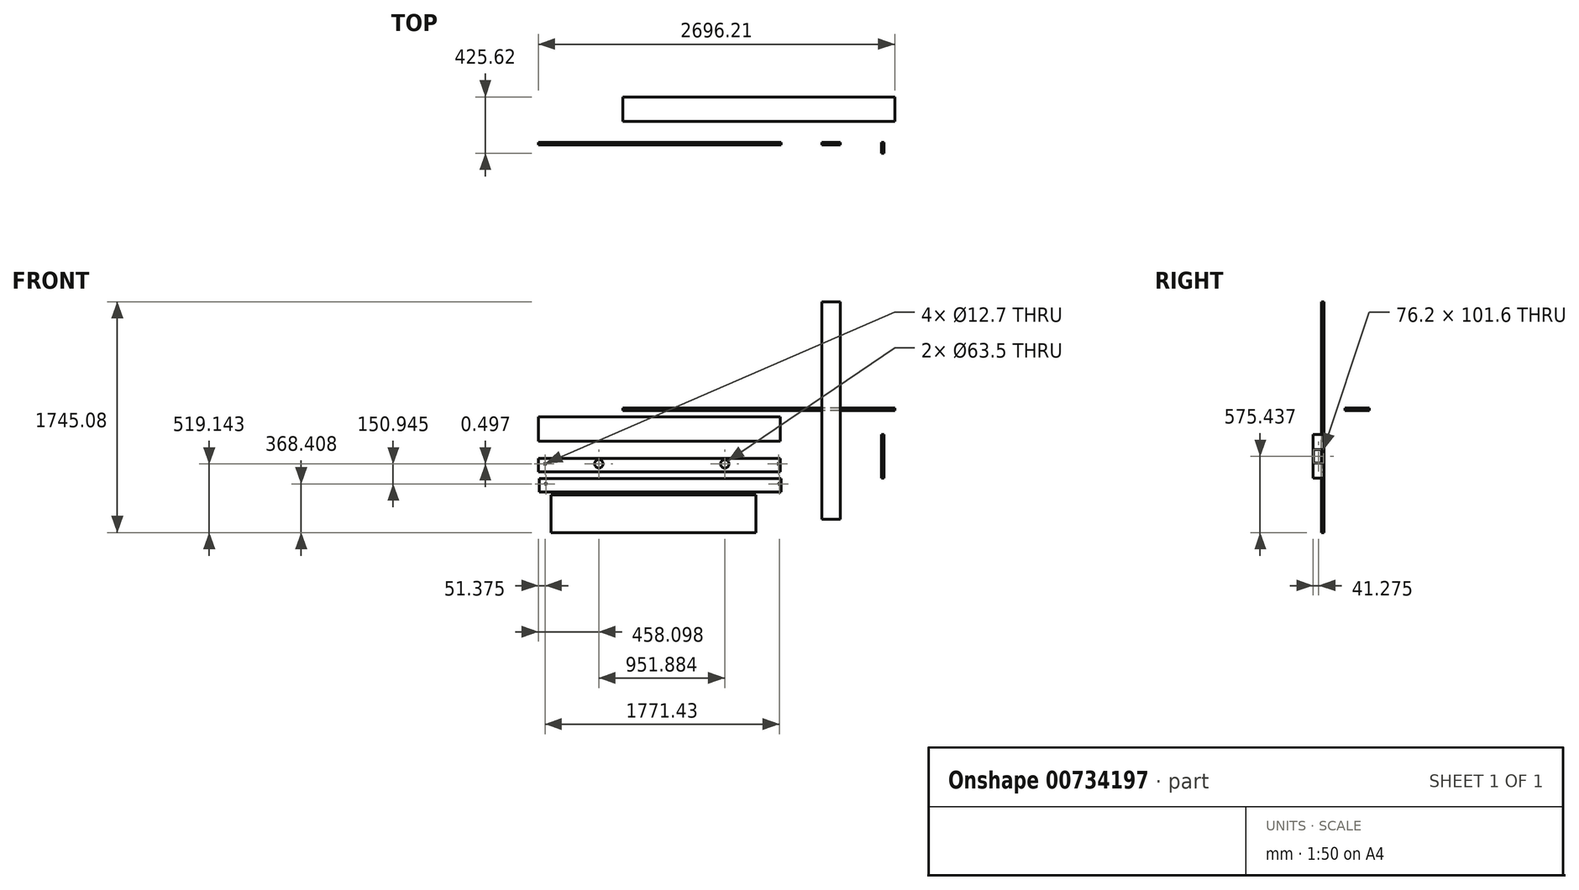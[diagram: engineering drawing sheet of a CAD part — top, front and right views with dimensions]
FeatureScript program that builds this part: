
annotation { "Feature Type Name" : "Feature", "Feature Type Description" : "" }
export const myFeature = defineFeature(function(context is Context, id is Id, definition is map)
    precondition{}
    {
        {
            var Q0;
            Q0=qCreatedBy(makeId("Front.planeOp"),FACE);
            var sketch = newSketch(context, id + "F0", { "sketchPlane" : qUnion([Q0])});
            skLineSegment(sketch, "E0.bottom", {"start": v(69.85, -822.32) * mm, "end": v(-69.85, -822.32) * mm});
            skLineSegment(sketch, "E0.top", {"start": v(69.85, 822.33) * mm, "end": v(-69.85, 822.33) * mm});
            skLineSegment(sketch, "E0.left", {"start": v(69.85, -822.32) * mm, "end": v(69.85, 822.33) * mm});
            skLineSegment(sketch, "E0.right", {"start": v(-69.85, -822.32) * mm, "end": v(-69.85, 822.33) * mm});
            skPoint(sketch, "E0.middle", {"position": v(0, 0) * mm});
            skSolve(sketch);
        }
        {
            var Q0;
            Q0=makeQuery(id+"F0.imprint","IMPRINT",FACE,{"disambiguationData":[TD([[makeQuery(id+"F0.imprint","IMPRINT",EDGE,{"derivedFrom":sQuery(id+"F0.wireOp",EDGE,"E0.bottom")}),-1.0]])]});
            extrude(context, id + "F1", {"entities" : qUnion([Q0]), "depth" : 19.05 * mm, "offsetDistance" : 25.4 * mm});
        }
        {
            var Q0;
            Q0=qCreatedBy(makeId("Top.planeOp"),FACE);
            var sketch = newSketch(context, id + "F2", { "sketchPlane" : qUnion([Q0])});
            skLineSegment(sketch, "E1.bottom", {"start": v(482.85, 158.92) * mm, "end": v(-1574.55, 158.92) * mm});
            skLineSegment(sketch, "E1.top", {"start": v(482.85, 343.07) * mm, "end": v(-1574.55, 343.07) * mm});
            skLineSegment(sketch, "E1.left", {"start": v(482.85, 158.92) * mm, "end": v(482.85, 343.07) * mm});
            skLineSegment(sketch, "E1.right", {"start": v(-1574.55, 158.92) * mm, "end": v(-1574.55, 343.07) * mm});
            skPoint(sketch, "E1.middle", {"position": v(-545.85, 251) * mm});
            skSolve(sketch);
        }
        {
            var Q0;
            Q0=makeQuery(id+"F2.imprint","IMPRINT",FACE,{"disambiguationData":[TD([[makeQuery(id+"F2.imprint","IMPRINT",EDGE,{"derivedFrom":sQuery(id+"F2.wireOp",EDGE,"E1.bottom")}),-1.0]])]});
            extrude(context, id + "F3", {"entities" : qUnion([Q0]), "depth" : 19.05 * mm, "offsetDistance" : 25.4 * mm});
        }
        {
            var Q0;
            Q0=qCreatedBy(makeId("Front.planeOp"),FACE);
            var sketch = newSketch(context, id + "F4", { "sketchPlane" : qUnion([Q0])});
            skLineSegment(sketch, "E2.bottom", {"start": v(-2213.36, -49.16) * mm, "end": v(-384.56, -49.16) * mm});
            skLineSegment(sketch, "E2.top", {"start": v(-2213.36, -233.3) * mm, "end": v(-384.56, -233.3) * mm});
            skLineSegment(sketch, "E2.left", {"start": v(-2213.36, -49.16) * mm, "end": v(-2213.36, -233.3) * mm});
            skLineSegment(sketch, "E2.right", {"start": v(-384.56, -49.16) * mm, "end": v(-384.56, -233.3) * mm});
            skSolve(sketch);
        }
        {
            var Q0;
            Q0 = qSketchRegion(id + "F4", true);
            extrude(context, id + "F5", {"entities" : qUnion([Q0]), "depth" : 19.05 * mm, "offsetDistance" : 25.4 * mm});
        }
        {
            var Q0;
            Q0=qCreatedBy(makeId("Front.planeOp"),FACE);
            var sketch = newSketch(context, id + "F6", { "sketchPlane" : qUnion([Q0])});
            skLineSegment(sketch, "E3.bottom", {"start": v(-2212.8, -362.16) * mm, "end": v(-384, -362.16) * mm});
            skLineSegment(sketch, "E3.top", {"start": v(-2212.8, -463.76) * mm, "end": v(-384, -463.76) * mm});
            skLineSegment(sketch, "E3.left", {"start": v(-2212.8, -362.16) * mm, "end": v(-2212.8, -463.76) * mm});
            skLineSegment(sketch, "E3.right", {"start": v(-384, -362.16) * mm, "end": v(-384, -463.76) * mm});
            skSolve(sketch);
        }
        {
            var Q0;
            Q0=makeQuery(id+"F6.imprint","IMPRINT",FACE,{"disambiguationData":[TD([[makeQuery(id+"F6.imprint","IMPRINT",EDGE,{"derivedFrom":sQuery(id+"F6.wireOp",EDGE,"E3.bottom")}),-1.0]])]});
            extrude(context, id + "F7", {"entities" : qUnion([Q0]), "depth" : 19.05 * mm, "offsetDistance" : 25.4 * mm});
        }
        {
            var Q0;
            Q0=qCreatedBy(makeId("Front.planeOp"),FACE);
            var sketch = newSketch(context, id + "F8", { "sketchPlane" : qUnion([Q0])});
            skLineSegment(sketch, "E4.bottom", {"start": v(381.95, -182.22) * mm, "end": v(401, -182.22) * mm});
            skLineSegment(sketch, "E4.top", {"start": v(381.95, -512.42) * mm, "end": v(401, -512.42) * mm});
            skLineSegment(sketch, "E4.left", {"start": v(381.95, -182.22) * mm, "end": v(381.95, -512.42) * mm});
            skLineSegment(sketch, "E4.right", {"start": v(401, -182.22) * mm, "end": v(401, -512.42) * mm});
            skSolve(sketch);
        }
        {
            var Q0;
            Q0 = qSketchRegion(id + "F8", true);
            extrude(context, id + "F9", {"entities" : qUnion([Q0]), "depth" : 82.55 * mm, "offsetDistance" : 25.4 * mm});
        }
        {
            var Q0;
            Q0=makeQuery(id+"F7.opExtrude","CAP_FACE",FACE,{"disambiguationData":[OSD([sQuery(id+"F6.wireOp",EDGE,"E3.bottom"),sQuery(id+"F6.wireOp",EDGE,"E3.top"),sQuery(id+"F6.wireOp",EDGE,"E3.left"),sQuery(id+"F6.wireOp",EDGE,"E3.right")])],"isStart":false});
            var sketch = newSketch(context, id + "F10", { "sketchPlane" : qUnion([Q0])});
            skLineSegment(sketch, "E5", {"start": v(-2212.8, -412.96) * mm, "end": v(-384, -412.96) * mm, "construction": true});
            skLineSegment(sketch, "E6", {"start": v(-434.8, -362.16) * mm, "end": v(-434.8, -463.76) * mm, "construction": true});
            skLineSegment(sketch, "E7", {"start": v(-2162, -362.16) * mm, "end": v(-2162, -463.76) * mm, "construction": true});
            skLineSegment(sketch, "E8", {"start": v(-1755.6, -362.16) * mm, "end": v(-1755.6, -463.76) * mm});
            skLineSegment(sketch, "E9", {"start": v(-841.2, -362.16) * mm, "end": v(-841.2, -463.76) * mm});
            skSolve(sketch);
        }
        {
            var Q0;
            Q0=makeQuery(id+"F10.imprint","IMPRINT",FACE,{"disambiguationData":[TD([[makeQuery(id+"F10.imprint","IMPRINT",EDGE,{"derivedFrom":makeQuery(id+"F7.opExtrude","CAP_EDGE",EDGE,{"disambiguationData":[OSD([sQuery(id+"F6.wireOp",EDGE,"E3.bottom")])],"isStart":false})}),-1.0]])]});
            var sketch = newSketch(context, id + "F11", { "sketchPlane" : qUnion([Q0])});
            skPoint(sketch, "E10", {"position": v(-2161.98, -403.4) * mm});
            skPoint(sketch, "E11", {"position": v(-396.66, -403.43) * mm});
            skSolve(sketch);
        }
        {
            var Q0;
            Q0=sQuery(id+"F11.wireOp",VERTEX,"E10");
            var Q1;
            Q1=sQuery(id+"F11.wireOp",VERTEX,"E11");
            var Q2;
            Q2=makeQuery(id+"F7.opExtrude","SWEPT_BODY",BODY,{"disambiguationData":[OSD([sQuery(id+"F6.wireOp",EDGE,"E3.bottom"),sQuery(id+"F6.wireOp",EDGE,"E3.top"),sQuery(id+"F6.wireOp",EDGE,"E3.left"),sQuery(id+"F6.wireOp",EDGE,"E3.right")])]});
            hole(context, id + "F12", {"style" : HoleStyle.SIMPLE, "endStyle" : HoleEndStyle.THROUGH, "holeDiameter" : 12.7 * mm, "majorDiameter" : 6.35 * mm, "isTappedThrough" : true, "tappedDepth" : 12.7 * mm, "tapClearance" : 3, "locations" : qUnion([Q0, Q1]), "scope" : qUnion([Q2])});
        }
        {
            var Q0;
            Q0=qCreatedBy(makeId("Front.planeOp"),FACE);
            var sketch = newSketch(context, id + "F13", { "sketchPlane" : qUnion([Q0])});
            skLineSegment(sketch, "E12.bottom", {"start": v(-2116.58, -637.01) * mm, "end": v(-567.18, -637.01) * mm});
            skLineSegment(sketch, "E12.top", {"start": v(-2116.58, -922.76) * mm, "end": v(-567.18, -922.76) * mm});
            skLineSegment(sketch, "E12.left", {"start": v(-2116.58, -637.01) * mm, "end": v(-2116.58, -922.76) * mm});
            skLineSegment(sketch, "E12.right", {"start": v(-567.18, -637.01) * mm, "end": v(-567.18, -922.76) * mm});
            skSolve(sketch);
        }
        {
            var Q0;
            Q0 = qSketchRegion(id + "F13", true);
            extrude(context, id + "F14", {"entities" : qUnion([Q0]), "depth" : 19.05 * mm, "offsetDistance" : 25.4 * mm});
        }
        {
            var Q0;
            {var subQ0=sQuery(id+"F10.wireOp",EDGE,"E9");Q0=makeQuery(id+"F10.imprint","IMPRINT",FACE,{"disambiguationData":[TD([[makeQuery(id+"F10.imprint","IMPRINT",EDGE,{"derivedFrom":subQ0}),1.0]])]});}
            var sketch = newSketch(context, id + "F15", { "sketchPlane" : qUnion([Q0])});
            skPoint(sketch, "E13", {"position": v(-803.38, -403.62) * mm});
            skPoint(sketch, "E14", {"position": v(-1755.26, -403.12) * mm});
            skSolve(sketch);
        }
        {
            var Q0;
            Q0=sQuery(id+"F15.wireOp",VERTEX,"E13");
            var Q1;
            Q1=sQuery(id+"F15.wireOp",VERTEX,"E14");
            var Q2;
            Q2=makeQuery(id+"F7.opExtrude","SWEPT_BODY",BODY,{"disambiguationData":[OSD([sQuery(id+"F6.wireOp",EDGE,"E3.bottom"),sQuery(id+"F6.wireOp",EDGE,"E3.top"),sQuery(id+"F6.wireOp",EDGE,"E3.left"),sQuery(id+"F6.wireOp",EDGE,"E3.right")])]});
            hole(context, id + "F16", {"style" : HoleStyle.SIMPLE, "endStyle" : HoleEndStyle.THROUGH, "holeDiameter" : 63.5 * mm, "majorDiameter" : 6.35 * mm, "isTappedThrough" : true, "tappedDepth" : 12.7 * mm, "tapClearance" : 3, "locations" : qUnion([Q0, Q1]), "scope" : qUnion([Q2])});
        }
        {
            var Q0;
            Q0=qCreatedBy(makeId("Front.planeOp"),FACE);
            var sketch = newSketch(context, id + "F17", { "sketchPlane" : qUnion([Q0])});
            skLineSegment(sketch, "E15.bottom", {"start": v(-2206.65, -513.08) * mm, "end": v(-377.85, -513.08) * mm});
            skLineSegment(sketch, "E15.top", {"start": v(-2206.65, -614.68) * mm, "end": v(-377.85, -614.68) * mm});
            skLineSegment(sketch, "E15.left", {"start": v(-2206.65, -513.08) * mm, "end": v(-2206.65, -614.68) * mm});
            skLineSegment(sketch, "E15.right", {"start": v(-377.85, -513.08) * mm, "end": v(-377.85, -614.68) * mm});
            skSolve(sketch);
        }
        {
            var Q0;
            Q0 = qSketchRegion(id + "F17", true);
            extrude(context, id + "F18", {"entities" : qUnion([Q0]), "depth" : 19.05 * mm, "offsetDistance" : 25.4 * mm});
        }
        {
            var Q0;
            Q0=makeQuery(id+"F18.opExtrude","CAP_FACE",FACE,{"disambiguationData":[OSD([sQuery(id+"F17.wireOp",EDGE,"E15.bottom"),sQuery(id+"F17.wireOp",EDGE,"E15.top"),sQuery(id+"F17.wireOp",EDGE,"E15.left"),sQuery(id+"F17.wireOp",EDGE,"E15.right")])],"isStart":false});
            var sketch = newSketch(context, id + "F19", { "sketchPlane" : qUnion([Q0])});
            skLineSegment(sketch, "E16", {"start": v(-2206.65, -563.88) * mm, "end": v(-377.85, -563.88) * mm, "construction": true});
            skLineSegment(sketch, "E17", {"start": v(-2155.85, -513.08) * mm, "end": v(-2155.85, -614.68) * mm, "construction": true});
            skLineSegment(sketch, "E18", {"start": v(-428.65, -513.08) * mm, "end": v(-428.65, -614.68) * mm, "construction": true});
            skSolve(sketch);
        }
        {
            var Q0;
            Q0=makeQuery(id+"F19.imprint","IMPRINT",FACE,{"disambiguationData":[TD([[makeQuery(id+"F19.imprint","IMPRINT",EDGE,{"derivedFrom":makeQuery(id+"F18.opExtrude","CAP_EDGE",EDGE,{"disambiguationData":[OSD([sQuery(id+"F17.wireOp",EDGE,"E15.bottom")])],"isStart":false})}),-1.0]])]});
            var sketch = newSketch(context, id + "F20", { "sketchPlane" : qUnion([Q0])});
            skPoint(sketch, "E19", {"position": v(-2155.85, -554.35) * mm});
            skPoint(sketch, "E20", {"position": v(-390.55, -554.35) * mm});
            skSolve(sketch);
        }
        {
            var Q0;
            Q0=sQuery(id+"F20.wireOp",VERTEX,"E19");
            var Q1;
            Q1=sQuery(id+"F20.wireOp",VERTEX,"E20");
            var Q2;
            Q2=makeQuery(id+"F18.opExtrude","SWEPT_BODY",BODY,{"disambiguationData":[OSD([sQuery(id+"F17.wireOp",EDGE,"E15.bottom"),sQuery(id+"F17.wireOp",EDGE,"E15.top"),sQuery(id+"F17.wireOp",EDGE,"E15.left"),sQuery(id+"F17.wireOp",EDGE,"E15.right")])]});
            hole(context, id + "F21", {"style" : HoleStyle.SIMPLE, "endStyle" : HoleEndStyle.THROUGH, "holeDiameter" : 12.7 * mm, "majorDiameter" : 6.35 * mm, "isTappedThrough" : true, "tappedDepth" : 12.7 * mm, "tapClearance" : 3, "locations" : qUnion([Q0, Q1]), "scope" : qUnion([Q2])});
        }
        {
            var Q0;
            Q0=makeQuery(id+"F9.opExtrude","SWEPT_FACE",FACE,{"disambiguationData":[OSD([sQuery(id+"F8.wireOp",EDGE,"E4.left")])]});
            var sketch = newSketch(context, id + "F22", { "sketchPlane" : qUnion([Q0])});
            skLineSegment(sketch, "E21.bottom", {"start": v(3.17, -296.52) * mm, "end": v(79.38, -296.52) * mm});
            skLineSegment(sketch, "E21.top", {"start": v(3.18, -398.12) * mm, "end": v(79.38, -398.12) * mm});
            skLineSegment(sketch, "E21.left", {"start": v(3.17, -296.52) * mm, "end": v(3.18, -398.12) * mm});
            skLineSegment(sketch, "E21.right", {"start": v(79.38, -296.52) * mm, "end": v(79.38, -398.12) * mm});
            skSolve(sketch);
        }
        {
            var Q0;
            Q0 = qSketchRegion(id + "F22", true);
            extrude(context, id + "F23", {"entities" : qUnion([Q0]), "operationType" : NewBodyOperationType.REMOVE, "endBound" : BoundingType.THROUGH_ALL, "oppositeDirection" : true, "depth" : 25.4 * mm, "offsetDistance" : 25.4 * mm});
        }
    });
